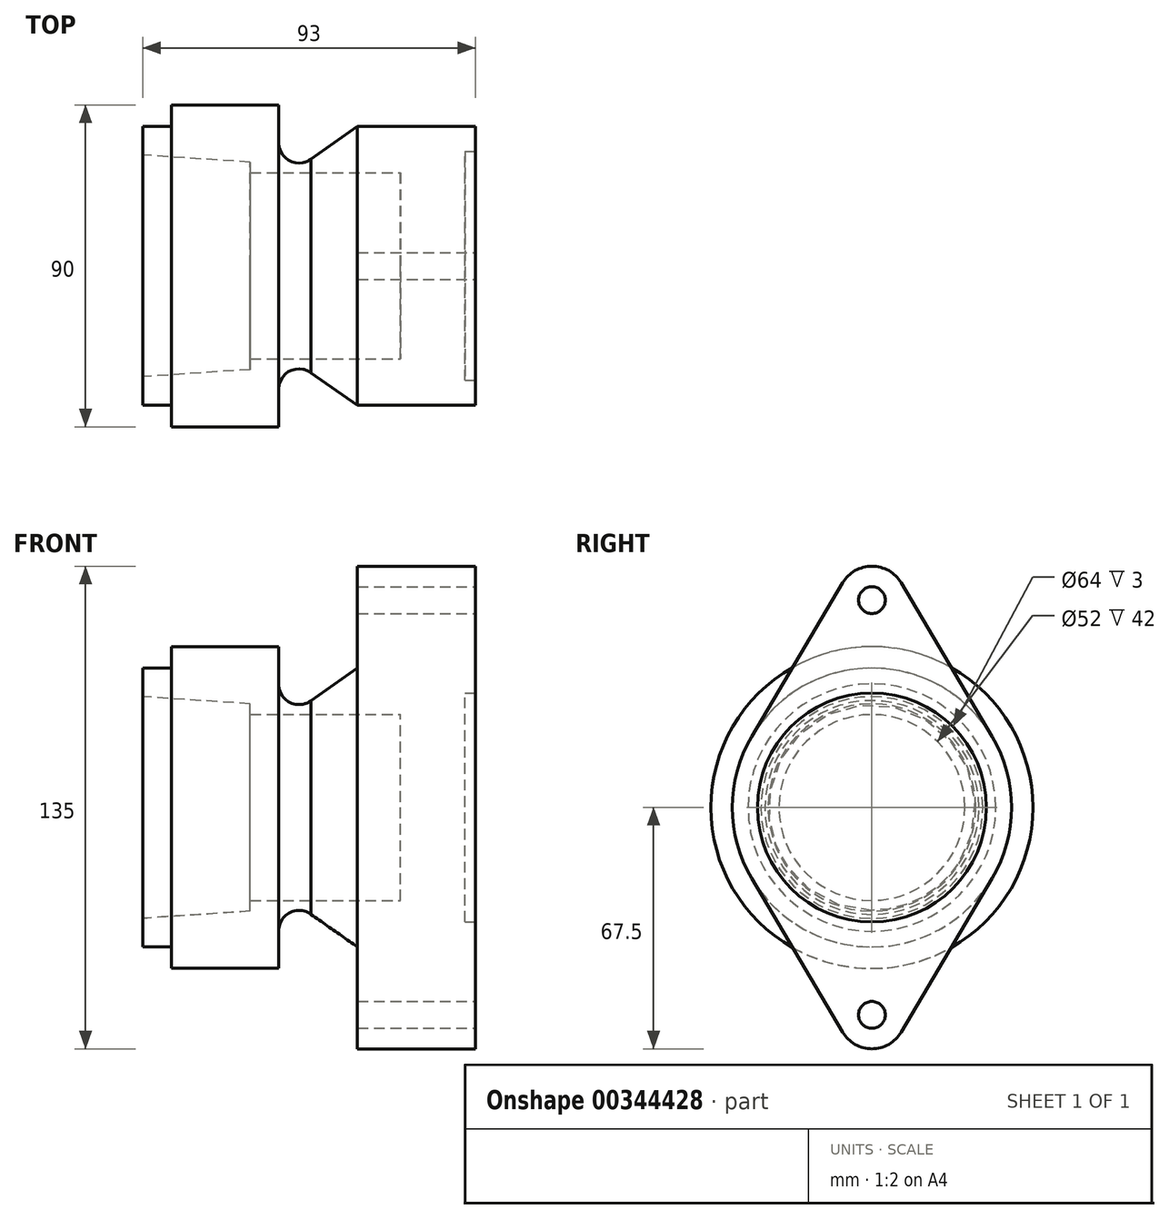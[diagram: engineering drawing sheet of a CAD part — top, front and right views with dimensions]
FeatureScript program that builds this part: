
annotation { "Feature Type Name" : "Feature", "Feature Type Description" : "" }
export const myFeature = defineFeature(function(context is Context, id is Id, definition is map)
    precondition{}
    {
        {
            var Q0;
            Q0=qCreatedBy(makeId("Front.planeOp"),FACE);
            var sketch = newSketch(context, id + "F0", { "sketchPlane" : qUnion([Q0])});
            skLineSegment(sketch, "E0", {"start": v(0, 0) * mm, "end": v(0, 26) * mm});
            skLineSegment(sketch, "E1", {"start": v(0, 26) * mm, "end": v(-42, 26) * mm});
            skLineSegment(sketch, "E2", {"start": v(-42, 26) * mm, "end": v(-42, 29) * mm});
            skLineSegment(sketch, "E3", {"start": v(-42, 29) * mm, "end": v(-72, 31) * mm});
            skLineSegment(sketch, "E4", {"start": v(-72, 31) * mm, "end": v(-72, 39) * mm});
            skLineSegment(sketch, "E5", {"start": v(-72, 39) * mm, "end": v(-64, 39) * mm});
            skLineSegment(sketch, "E6", {"start": v(-64, 39) * mm, "end": v(-64, 45) * mm});
            skLineSegment(sketch, "E7", {"start": v(21, 39) * mm, "end": v(21, 32) * mm});
            skPoint(sketch, "E8.start.orphan", {"position": v(66.52, 0) * mm});
            skLineSegment(sketch, "E9", {"start": v(21, 32) * mm, "end": v(18, 32) * mm});
            skLineSegment(sketch, "E10", {"start": v(18, 32) * mm, "end": v(18, 0) * mm});
            skLineSegment(sketch, "E11", {"start": v(18, 0) * mm, "end": v(0, 0) * mm});
            skPoint(sketch, "E12.start.orphan", {"position": v(-34, 45) * mm});
            skLineSegment(sketch, "E13", {"start": v(-64, 45) * mm, "end": v(-34, 45) * mm});
            skLineSegment(sketch, "E14", {"start": v(-12, 39) * mm, "end": v(21, 39) * mm});
            skLineSegment(sketch, "E15", {"start": v(-34, 45) * mm, "end": v(-34, 23.6) * mm, "construction": true});
            skLineSegment(sketch, "E16", {"start": v(-12, 39) * mm, "end": v(-34, 23.6) * mm, "construction": true});
            skLineSegment(sketch, "E17", {"start": v(-34, 23.6) * mm, "end": v(-15.2, 59.72) * mm, "construction": true});
            skArc(sketch, "E18", {"start": v(-34, 34.6) * mm, "mid": v(-30.97, 29.42) * mm, "end": v(-24.98, 29.91) * mm, "construction": true});
            skPoint(sketch, "E19", {"position": v(-30.97, 29.42) * mm});
            skLineSegment(sketch, "E20", {"start": v(-34, 45) * mm, "end": v(-34, 34.6) * mm});
            skArc(sketch, "E21", {"start": v(-34, 34.6) * mm, "mid": v(-30.97, 29.42) * mm, "end": v(-24.98, 29.91) * mm});
            skLineSegment(sketch, "E22", {"start": v(-24.98, 29.91) * mm, "end": v(-12, 39) * mm});
            skLineSegment(sketch, "E23", {"start": v(0, 0) * mm, "end": v(-144.39, 0) * mm, "construction": true});
            skSolve(sketch);
        }
        {
            var Q0;
            Q0=makeQuery(id+"F0.imprint","IMPRINT",FACE,{"disambiguationData":[TD([[makeQuery(id+"F0.imprint","IMPRINT",EDGE,{"derivedFrom":sQuery(id+"F0.wireOp",EDGE,"E0")}),-1.0]])]});
            var Q1;
            Q1=sQuery(id+"F0.wireOp",EDGE,"E23");
            revolve(context, id + "F1", {"entities" : qUnion([Q0]), "axis" : qUnion([Q1]), "revolveType" : RevolveType.FULL});
        }
        {
            var Q0;
            Q0=makeQuery(id+"F1.opRevolve","SWEPT_FACE",FACE,{"disambiguationData":[OSD([sQuery(id+"F0.wireOp",EDGE,"E7")])]});
            var sketch = newSketch(context, id + "F2", { "sketchPlane" : qUnion([Q0])});
            skLineSegment(sketch, "E24", {"start": v(-42.3, 58) * mm, "end": v(49.2, 58) * mm, "construction": true});
            skLineSegment(sketch, "E25", {"start": v(-48.17, -58) * mm, "end": v(50.18, -58) * mm, "construction": true});
            skLineSegment(sketch, "E26", {"start": v(0, 0) * mm, "end": v(0, 61.27) * mm, "construction": true});
            skLineSegment(sketch, "E27", {"start": v(0, 0) * mm, "end": v(0, -70.74) * mm, "construction": true});
            skPoint(sketch, "E28", {"position": v(0, 58) * mm});
            skPoint(sketch, "E29", {"position": v(0, -58) * mm});
            skArc(sketch, "E30", {"start": v(8.18, 62.83) * mm, "mid": v(0, 67.5) * mm, "end": v(-8.18, 62.83) * mm});
            skCircle(sketch, "E31", {"center": v(0, 58) * mm, "radius": 3.75 * mm});
            skArc(sketch, "E32", {"start": v(-8.18, -62.83) * mm, "mid": v(0, -67.5) * mm, "end": v(8.18, -62.83) * mm});
            skCircle(sketch, "E33", {"center": v(0, -58) * mm, "radius": 3.75 * mm});
            skPoint(sketch, "E34", {"position": v(3.75, 58) * mm});
            skPoint(sketch, "E35", {"position": v(9.5, 58) * mm});
            skPoint(sketch, "E36", {"position": v(9.5, -58) * mm});
            skPoint(sketch, "E37", {"position": v(3.75, -58) * mm});
            skLineSegment(sketch, "E38", {"start": v(-8.18, -62.83) * mm, "end": v(-33.58, -19.84) * mm});
            skLineSegment(sketch, "E39", {"start": v(8.13, -62.92) * mm, "end": v(33.58, -19.84) * mm});
            skLineSegment(sketch, "E40", {"start": v(-8.18, 62.83) * mm, "end": v(-33.58, 19.84) * mm});
            skLineSegment(sketch, "E41", {"start": v(8.18, 62.83) * mm, "end": v(33.58, 19.84) * mm});
            skPoint(sketch, "E42", {"position": v(-33.58, 19.84) * mm});
            skPoint(sketch, "E43", {"position": v(33.58, 19.84) * mm});
            skArc(sketch, "E44", {"start": v(33.58, 19.84) * mm, "mid": v(0, 39) * mm, "end": v(-33.58, 19.84) * mm});
            skArc(sketch, "E45.trimOffspring", {"start": v(-33.58, -19.84) * mm, "mid": v(0, -39) * mm, "end": v(33.58, -19.84) * mm});
            skSolve(sketch);
        }
        {
            var Q0;
            Q0=makeQuery(id+"F2.imprint","IMPRINT",FACE,{"disambiguationData":[TD([[makeQuery(id+"F2.imprint","IMPRINT",EDGE,{"derivedFrom":sQuery(id+"F2.wireOp",EDGE,"E30")}),1.0]])]});
            var Q1;
            {var subQ1=sQuery(id+"F2.wireOp",EDGE,"E32");Q1=makeQuery(id+"F2.imprint","IMPRINT",FACE,{"disambiguationData":[TD([[makeQuery(id+"F2.imprint","IMPRINT",EDGE,{"derivedFrom":subQ1}),1.0]])]});}
            extrude(context, id + "F3", {"entities" : qUnion([Q0, Q1]), "operationType" : NewBodyOperationType.ADD, "oppositeDirection" : true, "depth" : 33 * mm});
        }
    });
